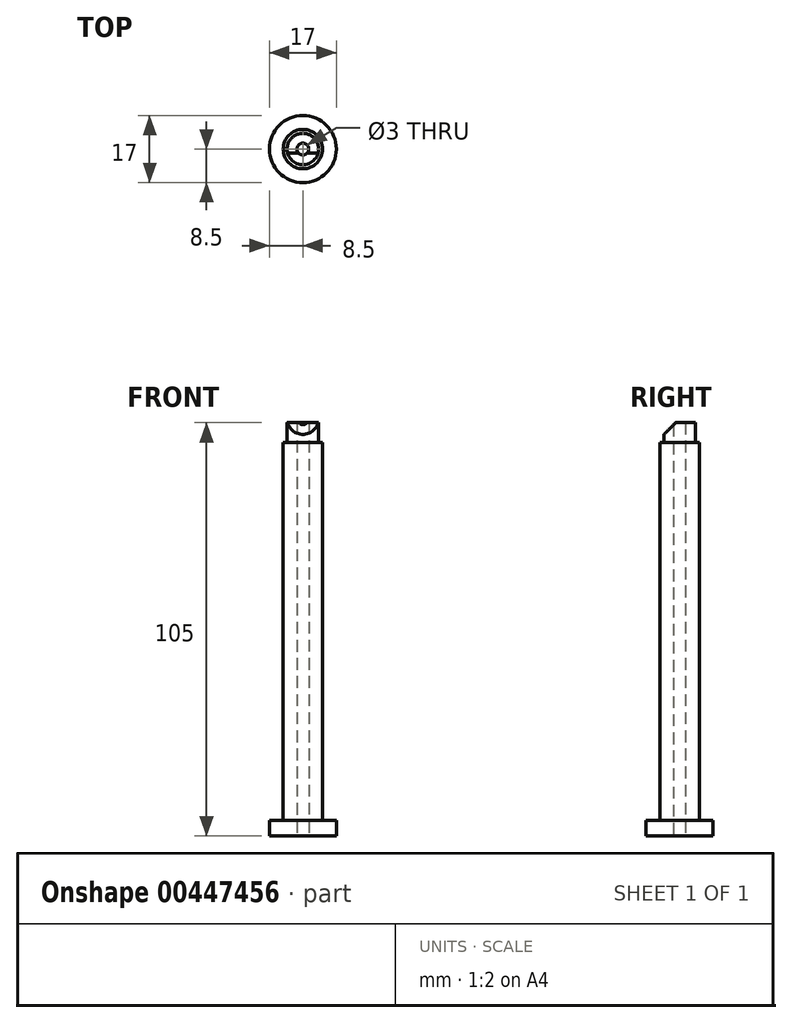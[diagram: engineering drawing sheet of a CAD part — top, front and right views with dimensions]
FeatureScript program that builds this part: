
annotation { "Feature Type Name" : "Feature", "Feature Type Description" : "" }
export const myFeature = defineFeature(function(context is Context, id is Id, definition is map)
    precondition{}
    {
        {
            var Q0;
            Q0=qCreatedBy(makeId("Top.planeOp"),FACE);
            var sketch = newSketch(context, id + "F0", { "sketchPlane" : qUnion([Q0])});
            skCircle(sketch, "E0", {"center": v(0, 0) * mm, "radius": 8.5 * mm});
            skSolve(sketch);
        }
        {
            var Q0;
            Q0=qSketchRegion(id+"F0",true);
            extrude(context, id + "F1", {"entities" : qUnion([Q0]), "depth" : 4 * mm});
        }
        {
            var Q0;
            Q0=qCreatedBy(makeId("Top.planeOp"),FACE);
            cPlane(context, id + "F2", {"entities" : qUnion([Q0]), "cplaneType" : CPlaneType.OFFSET, "offset" : 4 * mm, "width" : 150 * mm, "height" : 150 * mm});
        }
        {
            var Q0;
            Q0=qCreatedBy(makeId("Top.planeOp"),FACE);
            var sketch = newSketch(context, id + "F3", { "sketchPlane" : qUnion([Q0])});
            skCircle(sketch, "E1", {"center": v(0, 0) * mm, "radius": 5 * mm});
            skSolve(sketch);
        }
        {
            var Q0;
            Q0=qSketchRegion(id+"F3",true);
            extrude(context, id + "F4", {"entities" : qUnion([Q0]), "operationType" : NewBodyOperationType.ADD, "depth" : 100 * mm});
        }
        {
            var Q0;
            Q0=qCreatedBy(makeId("Right.planeOp"),FACE);
            var sketch = newSketch(context, id + "F5", { "sketchPlane" : qUnion([Q0])});
            skLineSegment(sketch, "E2.bottom", {"start": v(0, 105) * mm, "end": v(4, 105) * mm});
            skLineSegment(sketch, "E2.top", {"start": v(0, 100) * mm, "end": v(4, 100) * mm});
            skLineSegment(sketch, "E2.left", {"start": v(0, 105) * mm, "end": v(0, 100) * mm});
            skLineSegment(sketch, "E2.right", {"start": v(4, 105) * mm, "end": v(4, 100) * mm});
            skSolve(sketch);
        }
        {
            var Q0;
            Q0=makeQuery(id+"F5.imprint","IMPRINT",FACE,{"disambiguationData":[TD([[makeQuery(id+"F5.imprint","IMPRINT",EDGE,{"derivedFrom":sQuery(id+"F5.wireOp",EDGE,"E2.bottom")}),-1.0]])]});
            var Q1;
            Q1=sQuery(id+"F5.wireOp",EDGE,"E2.left");
            revolve(context, id + "F6", {"operationType" : NewBodyOperationType.ADD, "entities" : qUnion([Q0]), "axis" : qUnion([Q1]), "revolveType" : RevolveType.FULL});
        }
        {
            var Q0;
            Q0=qCreatedBy(id+"F2.planeOp",FACE);
            var sketch = newSketch(context, id + "F7", { "sketchPlane" : qUnion([Q0])});
            skLineSegment(sketch, "E3", {"start": v(8.44, 1) * mm, "end": v(8.44, -1) * mm});
            skSolve(sketch);
        }
        {
            var Q0;
            Q0=qCreatedBy(makeId("Right.planeOp"),FACE);
            var sketch = newSketch(context, id + "F8", { "sketchPlane" : qUnion([Q0])});
            skLineSegment(sketch, "E4", {"start": v(-5, 106) * mm, "end": v(0, 106) * mm});
            skLineSegment(sketch, "E5", {"start": v(0, 106) * mm, "end": v(-5, 101) * mm});
            skLineSegment(sketch, "E6", {"start": v(-5, 101) * mm, "end": v(-5, 106) * mm});
            skSolve(sketch);
        }
        {
            var Q0;
            Q0=makeQuery(id+"F8.imprint","IMPRINT",FACE,{"disambiguationData":[TD([[makeQuery(id+"F8.imprint","IMPRINT",EDGE,{"derivedFrom":sQuery(id+"F8.wireOp",EDGE,"E4")}),-1.0]])]});
            extrude(context, id + "F9", {"entities" : qUnion([Q0]), "operationType" : NewBodyOperationType.REMOVE, "endBound" : BoundingType.THROUGH_ALL, "oppositeDirection" : true, "depth" : 25 * mm, "hasSecondDirection" : true, "secondDirectionOppositeDirection" : false, "secondDirectionDepth" : 25 * mm});
        }
        {
            var Q0;
            Q0=makeQuery(id+"F1.opExtrude","CAP_FACE",FACE,{"disambiguationData":[OSD([sQuery(id+"F0.wireOp",EDGE,"E0")])],"isStart":true});
            var sketch = newSketch(context, id + "F10", { "sketchPlane" : qUnion([Q0])});
            skCircle(sketch, "E7", {"center": v(0, 0) * mm, "radius": 1.5 * mm});
            skSolve(sketch);
        }
        {
            var Q0;
            Q0 = qSketchRegion(id + "F10", true);
            extrude(context, id + "F11", {"entities" : qUnion([Q0]), "operationType" : NewBodyOperationType.REMOVE, "oppositeDirection" : true, "depth" : 110.8 * mm});
        }
    });
